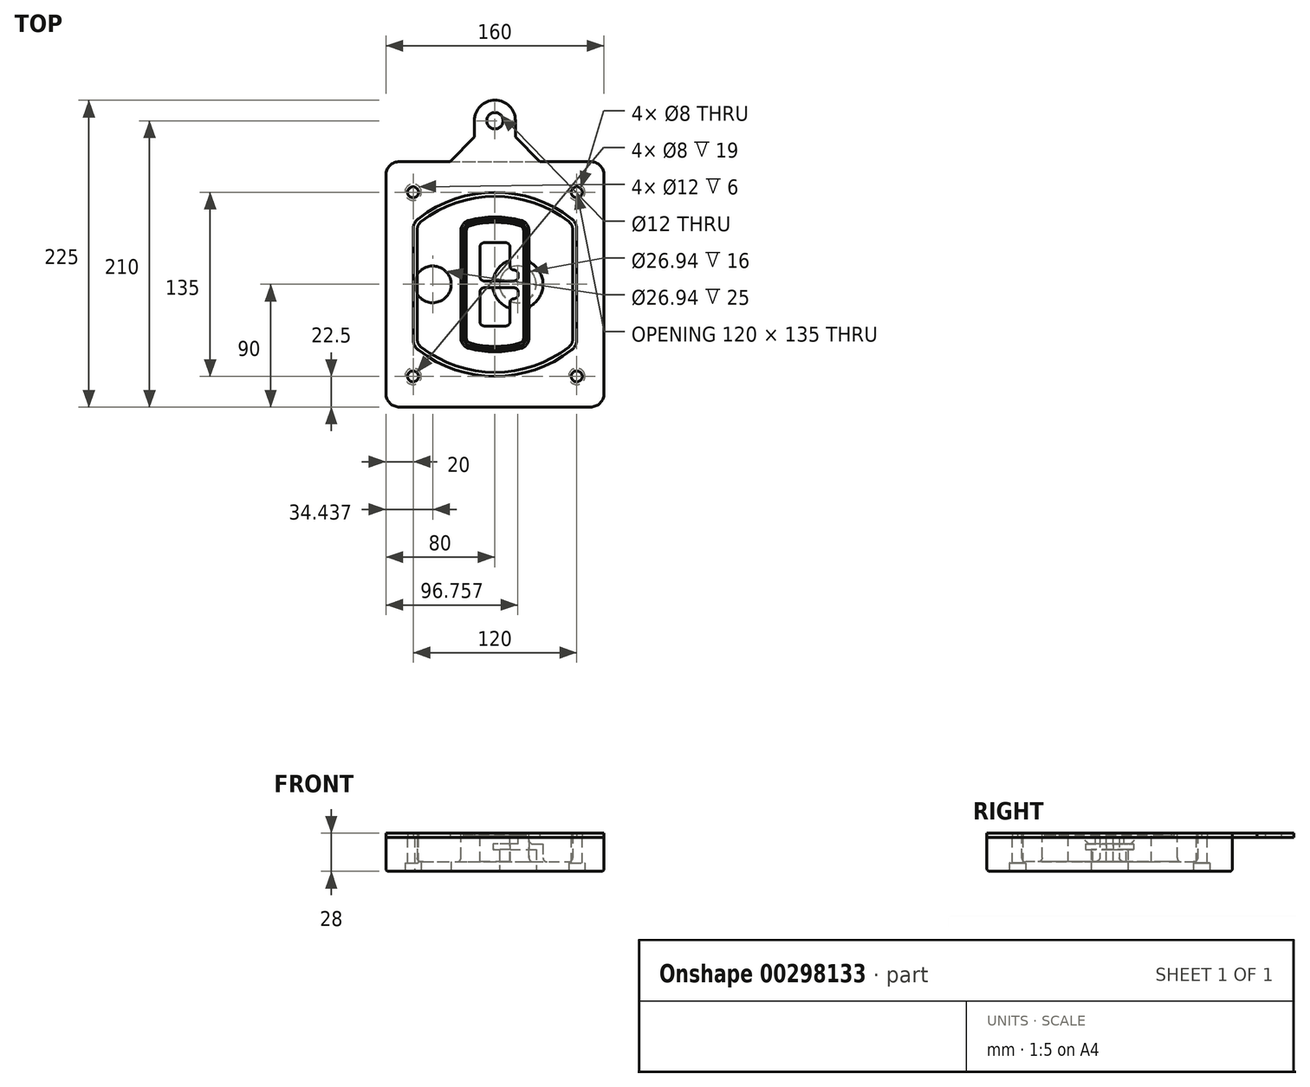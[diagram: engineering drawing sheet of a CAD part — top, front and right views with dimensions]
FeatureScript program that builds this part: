
annotation { "Feature Type Name" : "Feature", "Feature Type Description" : "" }
export const myFeature = defineFeature(function(context is Context, id is Id, definition is map)
    precondition{}
    {
        {
            var Q0;
            Q0=qCreatedBy(makeId("Top.planeOp"),FACE);
            var sketch = newSketch(context, id + "F0", { "sketchPlane" : qUnion([Q0])});
            skPoint(sketch, "E0.rect.middle", {"position": v(0, 0) * mm});
            skLineSegment(sketch, "E1.bottom", {"start": v(-70, -90) * mm, "end": v(70, -90) * mm});
            skLineSegment(sketch, "E1.top", {"start": v(-70, 90) * mm, "end": v(70, 90) * mm});
            skLineSegment(sketch, "E1.left", {"start": v(-80, -80) * mm, "end": v(-80, 80) * mm});
            skLineSegment(sketch, "E1.right", {"start": v(80, -80) * mm, "end": v(80, 80) * mm});
            skLineSegment(sketch, "E2", {"start": v(-80, 90) * mm, "end": v(80, -90) * mm, "construction": true});
            skLineSegment(sketch, "E3", {"start": v(80, 90) * mm, "end": v(-80, -90) * mm, "construction": true});
            skCircle(sketch, "E4", {"center": v(-60, 67.5) * mm, "radius": 4 * mm});
            skCircle(sketch, "E5", {"center": v(60, 67.5) * mm, "radius": 4 * mm});
            skCircle(sketch, "E6", {"center": v(60, -67.5) * mm, "radius": 4 * mm});
            skCircle(sketch, "E7", {"center": v(-60, -67.5) * mm, "radius": 4 * mm});
            skLineSegment(sketch, "E8", {"start": v(-60, 67.5) * mm, "end": v(60, 67.5) * mm, "construction": true});
            skLineSegment(sketch, "E9", {"start": v(60, 67.5) * mm, "end": v(60, -67.5) * mm, "construction": true});
            skLineSegment(sketch, "E10", {"start": v(60, -67.5) * mm, "end": v(-60, -67.5) * mm, "construction": true});
            skLineSegment(sketch, "E11", {"start": v(-60, -67.5) * mm, "end": v(-60, 67.5) * mm, "construction": true});
            skLineSegment(sketch, "E12", {"start": v(-60, 40.3) * mm, "end": v(-60, -40.3) * mm});
            skLineSegment(sketch, "E13", {"start": v(60, 40.3) * mm, "end": v(60, -40.3) * mm});
            skArc(sketch, "E14", {"start": v(56.15, 48.18) * mm, "mid": v(0, 67.5) * mm, "end": v(-56.15, 48.18) * mm});
            skArc(sketch, "E15", {"start": v(-56.15, -48.18) * mm, "mid": v(0, -67.5) * mm, "end": v(56.15, -48.18) * mm});
            skLineSegment(sketch, "E16", {"start": v(-60, 0) * mm, "end": v(60, 0) * mm, "construction": true});
            skPoint(sketch, "E17.visualSharp", {"position": v(-60, -45) * mm});
            skArc(sketch, "E17.filletArc", {"start": v(-60, -40.3) * mm, "mid": v(-58.99, -44.68) * mm, "end": v(-56.15, -48.18) * mm});
            skPoint(sketch, "E18.visualSharp", {"position": v(-60, 45) * mm});
            skArc(sketch, "E18.filletArc", {"start": v(-56.15, 48.18) * mm, "mid": v(-58.99, 44.68) * mm, "end": v(-60, 40.3) * mm});
            skPoint(sketch, "E19.visualSharp", {"position": v(60, 45) * mm});
            skArc(sketch, "E19.filletArc", {"start": v(60, 40.3) * mm, "mid": v(58.99, 44.68) * mm, "end": v(56.15, 48.18) * mm});
            skPoint(sketch, "E20.visualSharp", {"position": v(60, -45) * mm});
            skArc(sketch, "E20.filletArc", {"start": v(56.15, -48.18) * mm, "mid": v(58.99, -44.68) * mm, "end": v(60, -40.3) * mm});
            skPoint(sketch, "E21.visualSharp", {"position": v(-80, 90) * mm});
            skArc(sketch, "E21.filletArc", {"start": v(-70, 90) * mm, "mid": v(-77.07, 87.07) * mm, "end": v(-80, 80) * mm});
            skPoint(sketch, "E22.visualSharp", {"position": v(80, 90) * mm});
            skArc(sketch, "E22.filletArc", {"start": v(80, 80) * mm, "mid": v(77.07, 87.07) * mm, "end": v(70, 90) * mm});
            skPoint(sketch, "E23.visualSharp", {"position": v(80, -90) * mm});
            skArc(sketch, "E23.filletArc", {"start": v(70, -90) * mm, "mid": v(77.07, -87.07) * mm, "end": v(80, -80) * mm});
            skPoint(sketch, "E24.visualSharp", {"position": v(-80, -90) * mm});
            skArc(sketch, "E24.filletArc", {"start": v(-80, -80) * mm, "mid": v(-77.07, -87.07) * mm, "end": v(-70, -90) * mm});
            skArc(sketch, "E25.0", {"start": v(57, 40.3) * mm, "mid": v(56.3, 43.36) * mm, "end": v(54.3, 45.81) * mm});
            skLineSegment(sketch, "E25.1", {"start": v(57, 40.3) * mm, "end": v(57, -40.3) * mm});
            skArc(sketch, "E25.2", {"start": v(54.3, -45.81) * mm, "mid": v(56.3, -43.36) * mm, "end": v(57, -40.3) * mm});
            skArc(sketch, "E25.3", {"start": v(-54.3, -45.81) * mm, "mid": v(0, -64.5) * mm, "end": v(54.3, -45.81) * mm});
            skArc(sketch, "E25.4", {"start": v(-57, -40.3) * mm, "mid": v(-56.3, -43.36) * mm, "end": v(-54.3, -45.81) * mm});
            skArc(sketch, "E25.5", {"start": v(54.3, 45.81) * mm, "mid": v(0, 64.5) * mm, "end": v(-54.3, 45.81) * mm});
            skLineSegment(sketch, "E25.6", {"start": v(-57, 40.3) * mm, "end": v(-57, -40.3) * mm});
            skArc(sketch, "E25.7", {"start": v(-54.3, 45.81) * mm, "mid": v(-56.3, 43.36) * mm, "end": v(-57, 40.3) * mm});
            skArc(sketch, "E26.0", {"start": v(-58.62, 51.33) * mm, "mid": v(-62.58, 46.43) * mm, "end": v(-64, 40.3) * mm});
            skArc(sketch, "E26.1", {"start": v(58.62, 51.33) * mm, "mid": v(0, 71.5) * mm, "end": v(-58.62, 51.33) * mm});
            skArc(sketch, "E26.2", {"start": v(64, 40.3) * mm, "mid": v(62.58, 46.43) * mm, "end": v(58.62, 51.33) * mm});
            skLineSegment(sketch, "E26.3", {"start": v(64, 40.3) * mm, "end": v(64, -40.3) * mm});
            skArc(sketch, "E26.4", {"start": v(58.62, -51.33) * mm, "mid": v(62.58, -46.43) * mm, "end": v(64, -40.3) * mm});
            skLineSegment(sketch, "E26.5", {"start": v(-64, 40.3) * mm, "end": v(-64, -40.3) * mm});
            skArc(sketch, "E26.6", {"start": v(-58.62, -51.33) * mm, "mid": v(0, -71.5) * mm, "end": v(58.62, -51.33) * mm});
            skArc(sketch, "E26.7", {"start": v(-64, -40.3) * mm, "mid": v(-62.58, -46.43) * mm, "end": v(-58.62, -51.33) * mm});
            skSolve(sketch);
        }
        {
            var Q0;
            Q0=makeQuery(id+"F0.imprint","IMPRINT",FACE,{"disambiguationData":[TD([[makeQuery(id+"F0.imprint","IMPRINT",EDGE,{"derivedFrom":sQuery(id+"F0.wireOp",EDGE,"E1.bottom")}),1.0]])]});
            var Q1;
            Q1=makeQuery(id+"F0.imprint","IMPRINT",FACE,{"disambiguationData":[TD([[makeQuery(id+"F0.imprint","IMPRINT",EDGE,{"derivedFrom":sQuery(id+"F0.wireOp",EDGE,"E12")}),1.0]])]});
            var Q2;
            Q2=makeQuery(id+"F0.imprint","IMPRINT",FACE,{"disambiguationData":[TD([[makeQuery(id+"F0.imprint","IMPRINT",EDGE,{"derivedFrom":sQuery(id+"F0.wireOp",EDGE,"E25.0")}),1.0]])]});
            var Q3;
            Q3=makeQuery(id+"F0.imprint","IMPRINT",FACE,{"disambiguationData":[TD([[makeQuery(id+"F0.imprint","IMPRINT",EDGE,{"derivedFrom":sQuery(id+"F0.wireOp",EDGE,"E12")}),-1.0]])]});
            extrude(context, id + "F1", {"entities" : qUnion([Q0, Q1, Q2, Q3]), "oppositeDirection" : true, "depth" : 25 * mm});
        }
        {
            var Q0;
            Q0=makeQuery(id+"F0.imprint","IMPRINT",FACE,{"disambiguationData":[TD([[makeQuery(id+"F0.imprint","IMPRINT",EDGE,{"derivedFrom":sQuery(id+"F0.wireOp",EDGE,"E12")}),1.0]])]});
            extrude(context, id + "F2", {"entities" : qUnion([Q0]), "operationType" : NewBodyOperationType.ADD, "depth" : 3 * mm});
        }
        {
            var Q0;
            Q0=makeQuery(id+"F0.imprint","IMPRINT",FACE,{"disambiguationData":[TD([[makeQuery(id+"F0.imprint","IMPRINT",EDGE,{"derivedFrom":sQuery(id+"F0.wireOp",EDGE,"E25.0")}),1.0]])]});
            extrude(context, id + "F3", {"entities" : qUnion([Q0]), "operationType" : NewBodyOperationType.REMOVE, "oppositeDirection" : true, "depth" : 18 * mm});
        }
        {
            var Q0;
            Q0=makeQuery(id+"F2.opExtrude","CAP_FACE",FACE,{"disambiguationData":[OSD([sQuery(id+"F0.wireOp",EDGE,"E12"),sQuery(id+"F0.wireOp",EDGE,"E13"),sQuery(id+"F0.wireOp",EDGE,"E14"),sQuery(id+"F0.wireOp",EDGE,"E15"),sQuery(id+"F0.wireOp",EDGE,"E17.filletArc"),sQuery(id+"F0.wireOp",EDGE,"E18.filletArc"),sQuery(id+"F0.wireOp",EDGE,"E19.filletArc"),sQuery(id+"F0.wireOp",EDGE,"E20.filletArc"),sQuery(id+"F0.wireOp",EDGE,"E25.0"),sQuery(id+"F0.wireOp",EDGE,"E25.1"),sQuery(id+"F0.wireOp",EDGE,"E25.2"),sQuery(id+"F0.wireOp",EDGE,"E25.3"),sQuery(id+"F0.wireOp",EDGE,"E25.4"),sQuery(id+"F0.wireOp",EDGE,"E25.5"),sQuery(id+"F0.wireOp",EDGE,"E25.6"),sQuery(id+"F0.wireOp",EDGE,"E25.7")])],"isStart":false});
            var sketch = newSketch(context, id + "F4", { "sketchPlane" : qUnion([Q0])});
            skArc(sketch, "E27.0", {"start": v(-19.08, -46.97) * mm, "mid": v(0, -49.5) * mm, "end": v(19.08, -46.97) * mm});
            skArc(sketch, "E28.0", {"start": v(19.08, 46.97) * mm, "mid": v(0, 49.5) * mm, "end": v(-19.08, 46.97) * mm});
            skLineSegment(sketch, "E29", {"start": v(-25, 39.25) * mm, "end": v(-25, -39.25) * mm});
            skLineSegment(sketch, "E30", {"start": v(25, 39.25) * mm, "end": v(25, -39.25) * mm});
            skLineSegment(sketch, "E31", {"start": v(-25, 45.1) * mm, "end": v(25, 45.1) * mm, "construction": true});
            skLineSegment(sketch, "E32", {"start": v(-25, -45.1) * mm, "end": v(25, -45.1) * mm, "construction": true});
            skPoint(sketch, "E33.visualSharp", {"position": v(-25, 45.1) * mm});
            skArc(sketch, "E33.filletArc", {"start": v(-19.08, 46.97) * mm, "mid": v(-23.35, 44.11) * mm, "end": v(-25, 39.25) * mm});
            skPoint(sketch, "E34.visualSharp", {"position": v(25, 45.1) * mm});
            skArc(sketch, "E34.filletArc", {"start": v(25, 39.25) * mm, "mid": v(23.35, 44.11) * mm, "end": v(19.08, 46.97) * mm});
            skPoint(sketch, "E35.visualSharp", {"position": v(25, -45.1) * mm});
            skArc(sketch, "E35.filletArc", {"start": v(19.08, -46.97) * mm, "mid": v(23.35, -44.11) * mm, "end": v(25, -39.25) * mm});
            skPoint(sketch, "E36.visualSharp", {"position": v(-25, -45.1) * mm});
            skArc(sketch, "E36.filletArc", {"start": v(-25, -39.25) * mm, "mid": v(-23.35, -44.11) * mm, "end": v(-19.08, -46.97) * mm});
            skArc(sketch, "E37.0", {"start": v(54.3, 45.81) * mm, "mid": v(0, 64.5) * mm, "end": v(-54.3, 45.81) * mm});
            skArc(sketch, "E37.1", {"start": v(-54.3, 45.81) * mm, "mid": v(-56.3, 43.36) * mm, "end": v(-57, 40.3) * mm});
            skLineSegment(sketch, "E37.2", {"start": v(-57, 40.3) * mm, "end": v(-57, -40.3) * mm});
            skArc(sketch, "E37.3", {"start": v(-57, -40.3) * mm, "mid": v(-56.3, -43.36) * mm, "end": v(-54.3, -45.81) * mm});
            skArc(sketch, "E37.4", {"start": v(-54.3, -45.81) * mm, "mid": v(0, -64.5) * mm, "end": v(54.3, -45.81) * mm});
            skArc(sketch, "E37.5", {"start": v(54.3, -45.81) * mm, "mid": v(56.3, -43.36) * mm, "end": v(57, -40.3) * mm});
            skLineSegment(sketch, "E37.6", {"start": v(57, 40.3) * mm, "end": v(57, -40.3) * mm});
            skArc(sketch, "E37.7", {"start": v(57, 40.3) * mm, "mid": v(56.3, 43.36) * mm, "end": v(54.3, 45.81) * mm});
            skLineSegment(sketch, "E38.0", {"start": v(23, 39.25) * mm, "end": v(23, -39.25) * mm});
            skArc(sketch, "E38.1", {"start": v(18.56, -45.04) * mm, "mid": v(21.76, -42.9) * mm, "end": v(23, -39.25) * mm});
            skArc(sketch, "E38.2", {"start": v(-18.56, -45.04) * mm, "mid": v(0, -47.5) * mm, "end": v(18.56, -45.04) * mm});
            skArc(sketch, "E38.3", {"start": v(-23, -39.25) * mm, "mid": v(-21.76, -42.9) * mm, "end": v(-18.56, -45.04) * mm});
            skLineSegment(sketch, "E38.4", {"start": v(-23, 39.25) * mm, "end": v(-23, -39.25) * mm});
            skArc(sketch, "E38.5", {"start": v(23, 39.25) * mm, "mid": v(21.76, 42.9) * mm, "end": v(18.56, 45.04) * mm});
            skArc(sketch, "E38.6", {"start": v(-18.56, 45.04) * mm, "mid": v(-21.76, 42.9) * mm, "end": v(-23, 39.25) * mm});
            skArc(sketch, "E38.7", {"start": v(18.56, 45.04) * mm, "mid": v(0, 47.5) * mm, "end": v(-18.56, 45.04) * mm});
            skArc(sketch, "E39.0", {"start": v(21, 39.25) * mm, "mid": v(20.18, 41.68) * mm, "end": v(18.04, 43.1) * mm});
            skLineSegment(sketch, "E39.1", {"start": v(21, 39.25) * mm, "end": v(21, -39.25) * mm});
            skArc(sketch, "E39.2", {"start": v(18.04, -43.1) * mm, "mid": v(20.18, -41.68) * mm, "end": v(21, -39.25) * mm});
            skArc(sketch, "E39.3", {"start": v(-18.04, -43.1) * mm, "mid": v(0, -45.5) * mm, "end": v(18.04, -43.1) * mm});
            skArc(sketch, "E39.4", {"start": v(-21, -39.25) * mm, "mid": v(-20.18, -41.68) * mm, "end": v(-18.04, -43.1) * mm});
            skArc(sketch, "E39.5", {"start": v(18.04, 43.1) * mm, "mid": v(0, 45.5) * mm, "end": v(-18.04, 43.1) * mm});
            skLineSegment(sketch, "E39.6", {"start": v(-21, 39.25) * mm, "end": v(-21, -39.25) * mm});
            skArc(sketch, "E39.7", {"start": v(-18.04, 43.1) * mm, "mid": v(-20.18, 41.68) * mm, "end": v(-21, 39.25) * mm});
            skLineSegment(sketch, "E40", {"start": v(-25, 0) * mm, "end": v(25, 0) * mm, "construction": true});
            skLineSegment(sketch, "E41", {"start": v(-11, 5.5) * mm, "end": v(-11, 27.5) * mm});
            skLineSegment(sketch, "E42", {"start": v(-8, 30.5) * mm, "end": v(8, 30.5) * mm});
            skLineSegment(sketch, "E43", {"start": v(11, 27.5) * mm, "end": v(11, 13.5) * mm});
            skLineSegment(sketch, "E44", {"start": v(14, 10.5) * mm, "end": v(14, 10.5) * mm});
            skLineSegment(sketch, "E45", {"start": v(17, 7.5) * mm, "end": v(17, 5.5) * mm});
            skLineSegment(sketch, "E46", {"start": v(14, 2.5) * mm, "end": v(-8, 2.5) * mm});
            skPoint(sketch, "E47.visualSharp", {"position": v(-11, 30.5) * mm});
            skArc(sketch, "E47.filletArc", {"start": v(-8, 30.5) * mm, "mid": v(-10.12, 29.62) * mm, "end": v(-11, 27.5) * mm});
            skPoint(sketch, "E48.visualSharp", {"position": v(11, 30.5) * mm});
            skArc(sketch, "E48.filletArc", {"start": v(11, 27.5) * mm, "mid": v(10.12, 29.62) * mm, "end": v(8, 30.5) * mm});
            skPoint(sketch, "E49.visualSharp", {"position": v(11, 10.5) * mm});
            skArc(sketch, "E49.filletArc", {"start": v(11, 13.5) * mm, "mid": v(11.88, 11.38) * mm, "end": v(14, 10.5) * mm});
            skPoint(sketch, "E50.visualSharp", {"position": v(17, 10.5) * mm});
            skArc(sketch, "E50.filletArc", {"start": v(17, 7.5) * mm, "mid": v(16.12, 9.62) * mm, "end": v(14, 10.5) * mm});
            skPoint(sketch, "E51.visualSharp", {"position": v(17, 2.5) * mm});
            skArc(sketch, "E51.filletArc", {"start": v(14, 2.5) * mm, "mid": v(16.12, 3.38) * mm, "end": v(17, 5.5) * mm});
            skPoint(sketch, "E52.visualSharp", {"position": v(-11, 2.5) * mm});
            skArc(sketch, "E52.filletArc", {"start": v(-11, 5.5) * mm, "mid": v(-10.12, 3.38) * mm, "end": v(-8, 2.5) * mm});
            skLineSegment(sketch, "E53.0.MirrorCS", {"start": v(14, -2.5) * mm, "end": v(-8, -2.5) * mm});
            skArc(sketch, "E54.0.MirrorCS", {"start": v(-11, -5.5) * mm, "mid": v(-10.12, -3.38) * mm, "end": v(-8, -2.5) * mm});
            skLineSegment(sketch, "E55.0.MirrorCS", {"start": v(-11, -5.5) * mm, "end": v(-11, -27.5) * mm});
            skArc(sketch, "E56.0.MirrorCS", {"start": v(-8, -30.5) * mm, "mid": v(-10.12, -29.62) * mm, "end": v(-11, -27.5) * mm});
            skLineSegment(sketch, "E57.0.MirrorCS", {"start": v(-8, -30.5) * mm, "end": v(8, -30.5) * mm});
            skArc(sketch, "E58.0.MirrorCS", {"start": v(11, -27.5) * mm, "mid": v(10.12, -29.62) * mm, "end": v(8, -30.5) * mm});
            skLineSegment(sketch, "E59.0.MirrorCS", {"start": v(11, -27.5) * mm, "end": v(11, -13.5) * mm});
            skArc(sketch, "E60.0.MirrorCS", {"start": v(11, -13.5) * mm, "mid": v(11.88, -11.38) * mm, "end": v(14, -10.5) * mm});
            skArc(sketch, "E61.0.MirrorCS", {"start": v(17, -7.5) * mm, "mid": v(16.12, -9.62) * mm, "end": v(14, -10.5) * mm});
            skLineSegment(sketch, "E62.0.MirrorCS", {"start": v(17, -7.5) * mm, "end": v(17, -5.5) * mm});
            skArc(sketch, "E63.0.MirrorCS", {"start": v(14, -2.5) * mm, "mid": v(16.12, -3.38) * mm, "end": v(17, -5.5) * mm});
            skSolve(sketch);
        }
        {
            var Q0;
            Q0=makeQuery(id+"F4.imprint","IMPRINT",FACE,{"disambiguationData":[TD([[makeQuery(id+"F4.imprint","IMPRINT",EDGE,{"derivedFrom":sQuery(id+"F4.wireOp",EDGE,"E27.0")}),1.0]])]});
            var Q1;
            Q1=makeQuery(id+"F4.imprint","IMPRINT",FACE,{"disambiguationData":[TD([[makeQuery(id+"F4.imprint","IMPRINT",EDGE,{"derivedFrom":sQuery(id+"F4.wireOp",EDGE,"E38.0")}),-1.0]])]});
            var Q2;
            Q2=makeQuery(id+"F4.imprint","IMPRINT",FACE,{"disambiguationData":[TD([[makeQuery(id+"F4.imprint","IMPRINT",EDGE,{"derivedFrom":sQuery(id+"F4.wireOp",EDGE,"E39.0")}),1.0]])]});
            extrude(context, id + "F5", {"entities" : qUnion([Q0, Q1, Q2]), "operationType" : NewBodyOperationType.ADD, "endBound" : BoundingType.UP_TO_NEXT, "oppositeDirection" : true, "depth" : 25 * mm});
        }
        {
            var Q0;
            Q0=makeQuery(id+"F4.imprint","IMPRINT",FACE,{"disambiguationData":[TD([[makeQuery(id+"F4.imprint","IMPRINT",EDGE,{"derivedFrom":sQuery(id+"F4.wireOp",EDGE,"E38.0")}),-1.0]])]});
            extrude(context, id + "F6", {"entities" : qUnion([Q0]), "operationType" : NewBodyOperationType.REMOVE, "oppositeDirection" : true, "depth" : 2 * mm});
        }
        {
            var Q0;
            Q0=makeQuery(id+"F1.opExtrude","CAP_FACE",FACE,{"disambiguationData":[OSD([sQuery(id+"F0.wireOp",EDGE,"E1.bottom"),sQuery(id+"F0.wireOp",EDGE,"E1.top"),sQuery(id+"F0.wireOp",EDGE,"E1.left"),sQuery(id+"F0.wireOp",EDGE,"E1.right"),sQuery(id+"F0.wireOp",EDGE,"E4"),sQuery(id+"F0.wireOp",EDGE,"E5"),sQuery(id+"F0.wireOp",EDGE,"E6"),sQuery(id+"F0.wireOp",EDGE,"E7"),sQuery(id+"F0.wireOp",EDGE,"E21.filletArc"),sQuery(id+"F0.wireOp",EDGE,"E22.filletArc"),sQuery(id+"F0.wireOp",EDGE,"E23.filletArc"),sQuery(id+"F0.wireOp",EDGE,"E24.filletArc")])],"isStart":false});
            var sketch = newSketch(context, id + "F7", { "sketchPlane" : qUnion([Q0])});
            skCircle(sketch, "E64", {"center": v(16.76, 0) * mm, "radius": 13.47 * mm});
            skCircle(sketch, "E65", {"center": v(-45.56, 0) * mm, "radius": 13.47 * mm});
            skLineSegment(sketch, "E66", {"start": v(80, 0) * mm, "end": v(-80, 0) * mm});
            skCircle(sketch, "E67", {"center": v(16.76, 0) * mm, "radius": 18.47 * mm});
            skCircle(sketch, "E68", {"center": v(60, -67.5) * mm, "radius": 6 * mm});
            skCircle(sketch, "E69", {"center": v(-60, -67.5) * mm, "radius": 6 * mm});
            skCircle(sketch, "E70", {"center": v(-60, 67.5) * mm, "radius": 6 * mm});
            skCircle(sketch, "E71", {"center": v(60, 67.5) * mm, "radius": 6 * mm});
            skSolve(sketch);
        }
        {
            var Q0;
            {var subQ1=sQuery(id+"F7.wireOp",EDGE,"E66");var subQ4=sQuery(id+"F7.wireOp",EDGE,"E64");var subQ6=makeQuery(id+"F7.imprint","INTERSECT",VERTEX,{"disambiguationData":[OD(0.0)],"derivedFrom":[subQ4,subQ1]});Q0=makeQuery(id+"F7.imprint","IMPRINT",FACE,{"disambiguationData":[TD([[makeQuery(id+"F7.imprint","IMPRINT",EDGE,{"disambiguationData":[TD([[subQ6,-1.0]])],"derivedFrom":subQ4}),-1.0]])]});}
            var Q1;
            {var subQ0=sQuery(id+"F7.wireOp",EDGE,"E66");var subQ1=sQuery(id+"F7.wireOp",EDGE,"E64");var subQ3=makeQuery(id+"F7.imprint","INTERSECT",VERTEX,{"disambiguationData":[OD(0.0)],"derivedFrom":[subQ1,subQ0]});Q1=makeQuery(id+"F7.imprint","IMPRINT",FACE,{"disambiguationData":[TD([[makeQuery(id+"F7.imprint","IMPRINT",EDGE,{"disambiguationData":[TD([[subQ3,-1.0]])],"derivedFrom":subQ1}),1.0]])]});}
            var Q2;
            {var subQ0=sQuery(id+"F7.wireOp",EDGE,"E66");var subQ1=sQuery(id+"F7.wireOp",EDGE,"E64");var subQ3=makeQuery(id+"F7.imprint","INTERSECT",VERTEX,{"disambiguationData":[OD(0.0)],"derivedFrom":[subQ1,subQ0]});Q2=makeQuery(id+"F7.imprint","IMPRINT",FACE,{"disambiguationData":[TD([[makeQuery(id+"F7.imprint","IMPRINT",EDGE,{"disambiguationData":[TD([[subQ3,1.0]])],"derivedFrom":subQ1}),1.0]])]});}
            var Q3;
            {var subQ1=sQuery(id+"F7.wireOp",EDGE,"E66");var subQ4=sQuery(id+"F7.wireOp",EDGE,"E64");var subQ6=makeQuery(id+"F7.imprint","INTERSECT",VERTEX,{"disambiguationData":[OD(0.0)],"derivedFrom":[subQ4,subQ1]});Q3=makeQuery(id+"F7.imprint","IMPRINT",FACE,{"disambiguationData":[TD([[makeQuery(id+"F7.imprint","IMPRINT",EDGE,{"disambiguationData":[TD([[subQ6,1.0]])],"derivedFrom":subQ4}),-1.0]])]});}
            extrude(context, id + "F8", {"entities" : qUnion([Q0, Q1, Q2, Q3]), "operationType" : NewBodyOperationType.ADD, "oppositeDirection" : true, "depth" : 20 * mm});
        }
        {
            var Q0;
            {var subQ0=sQuery(id+"F7.wireOp",EDGE,"E66");var subQ1=sQuery(id+"F7.wireOp",EDGE,"E64");var subQ3=makeQuery(id+"F7.imprint","INTERSECT",VERTEX,{"disambiguationData":[OD(0.0)],"derivedFrom":[subQ1,subQ0]});Q0=makeQuery(id+"F7.imprint","IMPRINT",FACE,{"disambiguationData":[TD([[makeQuery(id+"F7.imprint","IMPRINT",EDGE,{"disambiguationData":[TD([[subQ3,-1.0]])],"derivedFrom":subQ1}),1.0]])]});}
            var Q1;
            {var subQ0=sQuery(id+"F7.wireOp",EDGE,"E66");var subQ1=sQuery(id+"F7.wireOp",EDGE,"E64");var subQ3=makeQuery(id+"F7.imprint","INTERSECT",VERTEX,{"disambiguationData":[OD(0.0)],"derivedFrom":[subQ1,subQ0]});Q1=makeQuery(id+"F7.imprint","IMPRINT",FACE,{"disambiguationData":[TD([[makeQuery(id+"F7.imprint","IMPRINT",EDGE,{"disambiguationData":[TD([[subQ3,1.0]])],"derivedFrom":subQ1}),1.0]])]});}
            extrude(context, id + "F9", {"entities" : qUnion([Q0, Q1]), "operationType" : NewBodyOperationType.REMOVE, "oppositeDirection" : true, "depth" : 16 * mm});
        }
        {
            var Q0;
            {var subQ0=sQuery(id+"F7.wireOp",EDGE,"E66");var subQ1=sQuery(id+"F7.wireOp",EDGE,"E65");var subQ3=makeQuery(id+"F7.imprint","INTERSECT",VERTEX,{"disambiguationData":[OD(0.0)],"derivedFrom":[subQ1,subQ0]});Q0=makeQuery(id+"F7.imprint","IMPRINT",FACE,{"disambiguationData":[TD([[makeQuery(id+"F7.imprint","IMPRINT",EDGE,{"disambiguationData":[TD([[subQ3,-1.0]])],"derivedFrom":subQ1}),1.0]])]});}
            var Q1;
            {var subQ0=sQuery(id+"F7.wireOp",EDGE,"E66");var subQ1=sQuery(id+"F7.wireOp",EDGE,"E65");var subQ3=makeQuery(id+"F7.imprint","INTERSECT",VERTEX,{"disambiguationData":[OD(0.0)],"derivedFrom":[subQ1,subQ0]});Q1=makeQuery(id+"F7.imprint","IMPRINT",FACE,{"disambiguationData":[TD([[makeQuery(id+"F7.imprint","IMPRINT",EDGE,{"disambiguationData":[TD([[subQ3,1.0]])],"derivedFrom":subQ1}),1.0]])]});}
            extrude(context, id + "F10", {"entities" : qUnion([Q0, Q1]), "operationType" : NewBodyOperationType.REMOVE, "oppositeDirection" : true, "depth" : 25 * mm});
        }
        {
            var Q0;
            Q0=makeQuery(id+"F7.imprint","IMPRINT",FACE,{"disambiguationData":[TD([[makeQuery(id+"F7.imprint","IMPRINT",EDGE,{"derivedFrom":sQuery(id+"F7.wireOp",EDGE,"E68")}),1.0]])]});
            var Q1;
            Q1=makeQuery(id+"F7.imprint","IMPRINT",FACE,{"disambiguationData":[TD([[makeQuery(id+"F7.imprint","IMPRINT",EDGE,{"derivedFrom":makeQuery(id+"F1.opExtrude","CAP_EDGE",EDGE,{"disambiguationData":[OSD([sQuery(id+"F0.wireOp",EDGE,"E5")])],"isStart":false})}),-1.0]])]});
            var Q2;
            Q2=makeQuery(id+"F7.imprint","IMPRINT",FACE,{"disambiguationData":[TD([[makeQuery(id+"F7.imprint","IMPRINT",EDGE,{"derivedFrom":sQuery(id+"F7.wireOp",EDGE,"E69")}),1.0]])]});
            var Q3;
            Q3=makeQuery(id+"F7.imprint","IMPRINT",FACE,{"disambiguationData":[TD([[makeQuery(id+"F7.imprint","IMPRINT",EDGE,{"derivedFrom":makeQuery(id+"F1.opExtrude","CAP_EDGE",EDGE,{"disambiguationData":[OSD([sQuery(id+"F0.wireOp",EDGE,"E4")])],"isStart":false})}),-1.0]])]});
            var Q4;
            Q4=makeQuery(id+"F7.imprint","IMPRINT",FACE,{"disambiguationData":[TD([[makeQuery(id+"F7.imprint","IMPRINT",EDGE,{"derivedFrom":sQuery(id+"F7.wireOp",EDGE,"E70")}),1.0]])]});
            var Q5;
            Q5=makeQuery(id+"F7.imprint","IMPRINT",FACE,{"disambiguationData":[TD([[makeQuery(id+"F7.imprint","IMPRINT",EDGE,{"derivedFrom":makeQuery(id+"F1.opExtrude","CAP_EDGE",EDGE,{"disambiguationData":[OSD([sQuery(id+"F0.wireOp",EDGE,"E7")])],"isStart":false})}),-1.0]])]});
            var Q6;
            Q6=makeQuery(id+"F7.imprint","IMPRINT",FACE,{"disambiguationData":[TD([[makeQuery(id+"F7.imprint","IMPRINT",EDGE,{"derivedFrom":sQuery(id+"F7.wireOp",EDGE,"E71")}),1.0]])]});
            var Q7;
            Q7=makeQuery(id+"F7.imprint","IMPRINT",FACE,{"disambiguationData":[TD([[makeQuery(id+"F7.imprint","IMPRINT",EDGE,{"derivedFrom":makeQuery(id+"F1.opExtrude","CAP_EDGE",EDGE,{"disambiguationData":[OSD([sQuery(id+"F0.wireOp",EDGE,"E6")])],"isStart":false})}),-1.0]])]});
            extrude(context, id + "F11", {"entities" : qUnion([Q0, Q1, Q2, Q3, Q4, Q5, Q6, Q7]), "operationType" : NewBodyOperationType.REMOVE, "oppositeDirection" : true, "depth" : 6 * mm});
        }
        {
            var Q0;
            Q0=makeQuery(id+"F9.boolean.opBoolean","COPY",FACE,{"derivedFrom":makeQuery(id+"F9.opExtrude","CAP_FACE",FACE,{"disambiguationData":[OSD([sQuery(id+"F7.wireOp",EDGE,"E64")])],"isStart":false})});
            var sketch = newSketch(context, id + "F12", { "sketchPlane" : qUnion([Q0])});
            skArc(sketch, "E72.0", {"start": v(11, 17.55) * mm, "mid": v(2.57, 11.82) * mm, "end": v(-1.54, 2.5) * mm});
            skArc(sketch, "E72.1", {"start": v(-1.54, -2.5) * mm, "mid": v(2.57, -11.82) * mm, "end": v(11, -17.55) * mm});
            skLineSegment(sketch, "E73", {"start": v(-1.54, -2.5) * mm, "end": v(14, -2.5) * mm});
            skLineSegment(sketch, "E74.0", {"start": v(14, 2.5) * mm, "end": v(-1.54, 2.5) * mm});
            skArc(sketch, "E74.1", {"start": v(14, 2.5) * mm, "mid": v(16.12, 3.38) * mm, "end": v(17, 5.5) * mm});
            skLineSegment(sketch, "E74.2", {"start": v(17, 7.5) * mm, "end": v(17, 5.5) * mm});
            skArc(sketch, "E74.3", {"start": v(17, 7.5) * mm, "mid": v(16.12, 9.62) * mm, "end": v(14, 10.5) * mm});
            skArc(sketch, "E74.4", {"start": v(11, 13.5) * mm, "mid": v(11.88, 11.38) * mm, "end": v(14, 10.5) * mm});
            skLineSegment(sketch, "E74.5", {"start": v(11, 17.55) * mm, "end": v(11, 13.5) * mm});
            skLineSegment(sketch, "E74.7", {"start": v(14, -2.5) * mm, "end": v(-1.54, -2.5) * mm});
            skArc(sketch, "E74.8", {"start": v(14, -2.5) * mm, "mid": v(16.12, -3.38) * mm, "end": v(17, -5.5) * mm});
            skLineSegment(sketch, "E74.9", {"start": v(17, -7.5) * mm, "end": v(17, -5.5) * mm});
            skArc(sketch, "E74.10", {"start": v(17, -7.5) * mm, "mid": v(16.12, -9.62) * mm, "end": v(14, -10.5) * mm});
            skArc(sketch, "E74.11", {"start": v(11, -13.5) * mm, "mid": v(11.88, -11.38) * mm, "end": v(14, -10.5) * mm});
            skLineSegment(sketch, "E74.12", {"start": v(11, -17.55) * mm, "end": v(11, -13.5) * mm});
            skPoint(sketch, "E75.orphan", {"position": v(11, -27.5) * mm});
            skPoint(sketch, "E76.orphan", {"position": v(-8, -2.5) * mm});
            skPoint(sketch, "E77.orphan", {"position": v(-8, 2.5) * mm});
            skPoint(sketch, "E78.orphan", {"position": v(11, 27.5) * mm});
            skSolve(sketch);
        }
        {
            var Q0;
            {var subQ7=sQuery(id+"F12.wireOp",EDGE,"E72.0");var subQ14=sQuery(id+"F12.wireOp",EDGE,"E72.1");var subQ16=sQuery(id+"F12.wireOp",EDGE,"E74.1");var subQ18=sQuery(id+"F12.wireOp",EDGE,"E74.8");Q0=qUnion([makeQuery(id+"F12.imprint","IMPRINT",FACE,{"disambiguationData":[TD([[makeQuery(id+"F12.imprint","IMPRINT",EDGE,{"derivedFrom":subQ7}),1.0]])]}),makeQuery(id+"F12.imprint","IMPRINT",FACE,{"disambiguationData":[TD([[makeQuery(id+"F12.imprint","IMPRINT",EDGE,{"derivedFrom":subQ14}),1.0]])]}),makeQuery(id+"F12.imprint","IMPRINT",FACE,{"disambiguationData":[TD([[makeQuery(id+"F12.imprint","IMPRINT",EDGE,{"derivedFrom":subQ16}),1.0]])]}),makeQuery(id+"F12.imprint","IMPRINT",FACE,{"disambiguationData":[TD([[makeQuery(id+"F12.imprint","IMPRINT",EDGE,{"derivedFrom":subQ18}),-1.0]])]})]);}
            var Q1;
            Q1=makeQuery(id+"F5.boolean.opBoolean","SPLIT",FACE,{"disambiguationData":[TD([makeQuery(id+"F5.opExtrude","SWEPT_FACE",FACE,{"disambiguationData":[OSD([sQuery(id+"F4.wireOp",EDGE,"E41")])]})])],"derivedFrom":makeQuery(id+"F3.boolean.opBoolean","COPY",FACE,{"derivedFrom":makeQuery(id+"F3.opExtrude","CAP_FACE",FACE,{"disambiguationData":[OSD([sQuery(id+"F0.wireOp",EDGE,"E25.0"),sQuery(id+"F0.wireOp",EDGE,"E25.1"),sQuery(id+"F0.wireOp",EDGE,"E25.2"),sQuery(id+"F0.wireOp",EDGE,"E25.3"),sQuery(id+"F0.wireOp",EDGE,"E25.4"),sQuery(id+"F0.wireOp",EDGE,"E25.5"),sQuery(id+"F0.wireOp",EDGE,"E25.6"),sQuery(id+"F0.wireOp",EDGE,"E25.7")])],"isStart":false})})});
            extrude(context, id + "F13", {"entities" : qUnion([Q0]), "operationType" : NewBodyOperationType.REMOVE, "endBound" : BoundingType.UP_TO_SURFACE, "endBoundEntityFace" : qUnion([Q1]), "depth" : 25 * mm});
        }
        {
            var Q0;
            Q0=makeQuery(id+"F3.boolean.opBoolean","COPY",EDGE,{"derivedFrom":makeQuery(id+"F3.opExtrude","CAP_EDGE",EDGE,{"disambiguationData":[OSD([sQuery(id+"F0.wireOp",EDGE,"E25.6")])],"isStart":false})});
            var Q1;
            Q1=makeQuery(id+"F8.boolean.opBoolean","INTERSECT",EDGE,{"derivedFrom":[makeQuery(id+"F5.opExtrude","SWEPT_FACE",FACE,{"disambiguationData":[OSD([sQuery(id+"F4.wireOp",EDGE,"E30")])]}),makeQuery(id+"F8.opExtrude","CAP_FACE",FACE,{"disambiguationData":[OSD([sQuery(id+"F7.wireOp",EDGE,"E67")])],"isStart":false})]});
            var Q2;
            Q2=makeQuery(id+"F8.boolean.opBoolean","INTERSECT",EDGE,{"disambiguationData":[OD(1.0)],"derivedFrom":[makeQuery(id+"F5.opExtrude","SWEPT_FACE",FACE,{"disambiguationData":[OSD([sQuery(id+"F4.wireOp",EDGE,"E30")])]}),makeQuery(id+"F8.opExtrude","SWEPT_FACE",FACE,{"disambiguationData":[OSD([sQuery(id+"F7.wireOp",EDGE,"E67")])]})]});
            var Q3;
            {var subQ0=sQuery(id+"F4.wireOp",EDGE,"E30");Q3=makeQuery(id+"F8.boolean.opBoolean","SPLIT",EDGE,{"disambiguationData":[TD([makeQuery(id+"F5.opExtrude","SWEPT_FACE",FACE,{"disambiguationData":[OSD([sQuery(id+"F4.wireOp",EDGE,"E35.filletArc")])]})])],"derivedFrom":makeQuery(id+"F5.opExtrude","CAP_EDGE",EDGE,{"disambiguationData":[OSD([subQ0])],"isStart":false})});}
            var Q4;
            {var subQ0=sQuery(id+"F0.wireOp",EDGE,"E25.7");var subQ1=sQuery(id+"F0.wireOp",EDGE,"E25.1");var subQ2=sQuery(id+"F0.wireOp",EDGE,"E25.6");var subQ3=sQuery(id+"F0.wireOp",EDGE,"E25.5");var subQ4=sQuery(id+"F0.wireOp",EDGE,"E25.4");var subQ5=sQuery(id+"F0.wireOp",EDGE,"E25.0");var subQ6=sQuery(id+"F0.wireOp",EDGE,"E25.2");var subQ7=sQuery(id+"F0.wireOp",EDGE,"E25.3");Q4=makeQuery(id+"F8.boolean.opBoolean","INTERSECT",EDGE,{"derivedFrom":[makeQuery(id+"F5.boolean.opBoolean","SPLIT",FACE,{"disambiguationData":[TD([makeQuery(id+"F2.opExtrude","SWEPT_FACE",FACE,{"disambiguationData":[OSD([subQ5])]})])],"derivedFrom":makeQuery(id+"F3.boolean.opBoolean","COPY",FACE,{"derivedFrom":makeQuery(id+"F3.opExtrude","CAP_FACE",FACE,{"disambiguationData":[OSD([subQ5,subQ1,subQ6,subQ7,subQ4,subQ3,subQ2,subQ0])],"isStart":false})})}),makeQuery(id+"F8.opExtrude","SWEPT_FACE",FACE,{"disambiguationData":[OSD([sQuery(id+"F7.wireOp",EDGE,"E67")])]})]});}
            var Q5;
            Q5=makeQuery(id+"F8.boolean.opBoolean","INTERSECT",EDGE,{"disambiguationData":[OD(0.0)],"derivedFrom":[makeQuery(id+"F5.opExtrude","SWEPT_FACE",FACE,{"disambiguationData":[OSD([sQuery(id+"F4.wireOp",EDGE,"E30")])]}),makeQuery(id+"F8.opExtrude","SWEPT_FACE",FACE,{"disambiguationData":[OSD([sQuery(id+"F7.wireOp",EDGE,"E67")])]})]});
            fillet(context, id + "F14", {"entities" : qUnion([Q0, Q1, Q2, Q3, Q4, Q5]), "radius" : 3 * mm, "tangentPropagation" : true, "allowEdgeOverflow" : false});
        }
        {
            var Q0;
            Q0=makeQuery(id+"F1.opExtrude","CAP_EDGE",EDGE,{"disambiguationData":[OSD([sQuery(id+"F0.wireOp",EDGE,"E1.bottom")])],"isStart":false});
            fillet(context, id + "F15", {"entities" : qUnion([Q0]), "radius" : 2 * mm, "tangentPropagation" : true, "allowEdgeOverflow" : false});
        }
        {
            var Q0;
            {var subQ0=sQuery(id+"F0.wireOp",EDGE,"E21.filletArc");var subQ1=sQuery(id+"F0.wireOp",EDGE,"E7");var subQ2=sQuery(id+"F0.wireOp",EDGE,"E6");var subQ3=sQuery(id+"F0.wireOp",EDGE,"E5");var subQ4=sQuery(id+"F0.wireOp",EDGE,"E4");var subQ5=sQuery(id+"F0.wireOp",EDGE,"E22.filletArc");var subQ6=sQuery(id+"F0.wireOp",EDGE,"E1.bottom");var subQ7=sQuery(id+"F0.wireOp",EDGE,"E1.right");var subQ8=sQuery(id+"F0.wireOp",EDGE,"E1.top");var subQ9=sQuery(id+"F0.wireOp",EDGE,"E1.left");var subQ10=sQuery(id+"F0.wireOp",EDGE,"E23.filletArc");var subQ11=sQuery(id+"F0.wireOp",EDGE,"E24.filletArc");Q0=makeQuery(id+"F2.boolean.opBoolean","SPLIT",FACE,{"disambiguationData":[TD([makeQuery(id+"F1.opExtrude","SWEPT_FACE",FACE,{"disambiguationData":[OSD([subQ6])]})])],"derivedFrom":makeQuery(id+"F1.opExtrude","CAP_FACE",FACE,{"disambiguationData":[OSD([subQ6,subQ8,subQ9,subQ7,subQ4,subQ3,subQ2,subQ1,subQ0,subQ5,subQ10,subQ11])],"isStart":true})});}
            var sketch = newSketch(context, id + "F16", { "sketchPlane" : qUnion([Q0])});
            skLineSegment(sketch, "E79", {"start": v(0, 90) * mm, "end": v(0, 120) * mm, "construction": true});
            skCircle(sketch, "E80", {"center": v(0, 120) * mm, "radius": 6 * mm});
            skArc(sketch, "E81", {"start": v(15, 120) * mm, "mid": v(0, 135) * mm, "end": v(-15, 120) * mm});
            skLineSegment(sketch, "E82", {"start": v(-15, 120) * mm, "end": v(-15, 108) * mm});
            skLineSegment(sketch, "E83", {"start": v(15, 120) * mm, "end": v(15, 108) * mm});
            skLineSegment(sketch, "E84", {"start": v(15, 108) * mm, "end": v(33, 90) * mm});
            skLineSegment(sketch, "E85", {"start": v(-15, 108) * mm, "end": v(-33, 90) * mm});
            skLineSegment(sketch, "E86", {"start": v(-80, 0) * mm, "end": v(80, 0) * mm, "construction": true});
            skLineSegment(sketch, "E87.MirrorCS", {"start": v(0, -90) * mm, "end": v(0, -120) * mm, "construction": true});
            skArc(sketch, "E88.MirrorCS", {"start": v(15, -120) * mm, "mid": v(0, -135) * mm, "end": v(-15, -120) * mm});
            skLineSegment(sketch, "E89.MirrorCS", {"start": v(15, -120) * mm, "end": v(15, -108) * mm});
            skLineSegment(sketch, "E90.MirrorCS", {"start": v(-15, -120) * mm, "end": v(-15, -108) * mm});
            skLineSegment(sketch, "E91.MirrorCS", {"start": v(15, -108) * mm, "end": v(33, -90) * mm});
            skCircle(sketch, "E92.MirrorC", {"center": v(0, -120) * mm, "radius": 6 * mm});
            skLineSegment(sketch, "E93.MirrorCS", {"start": v(-15, -108) * mm, "end": v(-33, -90) * mm});
            skSolve(sketch);
        }
        {
            var Q0;
            Q0=makeQuery(id+"F16.imprint","IMPRINT",FACE,{"disambiguationData":[TD([[makeQuery(id+"F16.imprint","IMPRINT",EDGE,{"derivedFrom":sQuery(id+"F16.wireOp",EDGE,"E80")}),-1.0]])]});
            var Q1;
            Q1=makeQuery(id+"F16.imprint","IMPRINT",FACE,{"disambiguationData":[TD([[makeQuery(id+"F16.imprint","IMPRINT",EDGE,{"derivedFrom":makeQuery(id+"F1.opExtrude","CAP_EDGE",EDGE,{"disambiguationData":[OSD([sQuery(id+"F0.wireOp",EDGE,"E1.left")])],"isStart":true})}),-1.0]])]});
            var Q2;
            Q2=makeQuery(id+"F16.imprint","IMPRINT",FACE,{"disambiguationData":[TD([[makeQuery(id+"F16.imprint","IMPRINT",EDGE,{"derivedFrom":sQuery(id+"F16.wireOp",EDGE,"E88.MirrorCS")}),-1.0]])]});
            var Q3;
            Q3=makeQuery(id+"F2.opExtrude","CAP_FACE",FACE,{"disambiguationData":[OSD([sQuery(id+"F0.wireOp",EDGE,"E12"),sQuery(id+"F0.wireOp",EDGE,"E13"),sQuery(id+"F0.wireOp",EDGE,"E14"),sQuery(id+"F0.wireOp",EDGE,"E15"),sQuery(id+"F0.wireOp",EDGE,"E17.filletArc"),sQuery(id+"F0.wireOp",EDGE,"E18.filletArc"),sQuery(id+"F0.wireOp",EDGE,"E19.filletArc"),sQuery(id+"F0.wireOp",EDGE,"E20.filletArc"),sQuery(id+"F0.wireOp",EDGE,"E25.0"),sQuery(id+"F0.wireOp",EDGE,"E25.1"),sQuery(id+"F0.wireOp",EDGE,"E25.2"),sQuery(id+"F0.wireOp",EDGE,"E25.3"),sQuery(id+"F0.wireOp",EDGE,"E25.4"),sQuery(id+"F0.wireOp",EDGE,"E25.5"),sQuery(id+"F0.wireOp",EDGE,"E25.6"),sQuery(id+"F0.wireOp",EDGE,"E25.7")])],"isStart":false});
            extrude(context, id + "F17", {"entities" : qUnion([Q0, Q1, Q2]), "endBound" : BoundingType.UP_TO_SURFACE, "endBoundEntityFace" : qUnion([Q3]), "depth" : 25 * mm});
        }
    });
